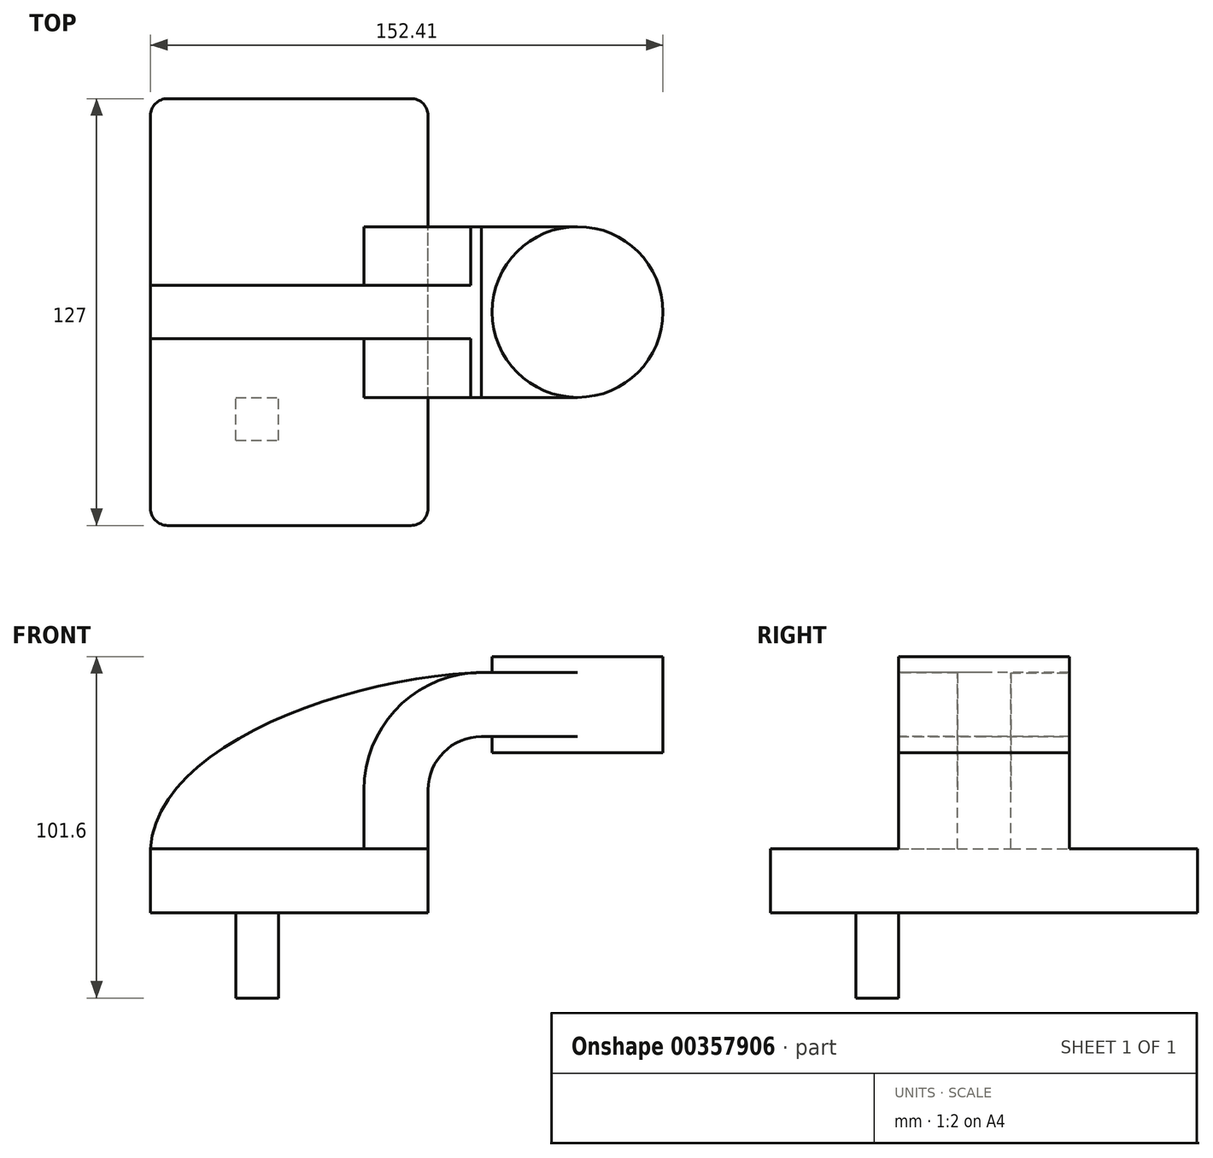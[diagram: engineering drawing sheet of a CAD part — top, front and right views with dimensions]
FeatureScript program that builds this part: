
annotation { "Feature Type Name" : "Feature", "Feature Type Description" : "" }
export const myFeature = defineFeature(function(context is Context, id is Id, definition is map)
    precondition{}
    {
        {
            var Q0;
            Q0=qCreatedBy(makeId("Front.planeOp"),FACE);
            var sketch = newSketch(context, id + "F0", { "sketchPlane" : qUnion([Q0])});
            skLineSegment(sketch, "E0.rect.bottom", {"start": v(-41.28, 9.52) * mm, "end": v(41.28, 9.52) * mm});
            skLineSegment(sketch, "E0.rect.top", {"start": v(-41.28, -9.52) * mm, "end": v(41.28, -9.52) * mm});
            skLineSegment(sketch, "E0.rect.left", {"start": v(-41.28, 9.52) * mm, "end": v(-41.28, -9.52) * mm});
            skLineSegment(sketch, "E0.rect.right", {"start": v(41.28, 9.52) * mm, "end": v(41.28, -9.52) * mm});
            skPoint(sketch, "E0.rect.middle", {"position": v(0, 0) * mm});
            skLineSegment(sketch, "E1", {"start": v(41.28, 9.52) * mm, "end": v(41.28, 27) * mm});
            skArc(sketch, "E2", {"start": v(41.28, 27) * mm, "mid": v(45.92, 38.23) * mm, "end": v(57.15, 42.88) * mm});
            skLineSegment(sketch, "E3", {"start": v(57.15, 42.88) * mm, "end": v(85.72, 42.88) * mm});
            skLineSegment(sketch, "E4.rect.bottom", {"start": v(60.32, 38.1) * mm, "end": v(111.12, 38.1) * mm});
            skLineSegment(sketch, "E4.rect.top", {"start": v(60.32, 66.68) * mm, "end": v(111.12, 66.68) * mm});
            skLineSegment(sketch, "E4.rect.left", {"start": v(60.32, 38.1) * mm, "end": v(60.32, 66.68) * mm});
            skLineSegment(sketch, "E4.rect.right", {"start": v(111.13, 38.1) * mm, "end": v(111.12, 66.68) * mm});
            skPoint(sketch, "E4.rect.middle", {"position": v(85.72, 52.39) * mm});
            skLineSegment(sketch, "E5.0", {"start": v(57.15, 61.93) * mm, "end": v(85.72, 61.93) * mm});
            skArc(sketch, "E5.1", {"start": v(22.23, 27) * mm, "mid": v(32.45, 51.7) * mm, "end": v(57.15, 61.93) * mm});
            skLineSegment(sketch, "E5.2", {"start": v(22.23, 9.52) * mm, "end": v(22.23, 27) * mm});
            skLineSegment(sketch, "E6", {"start": v(85.72, 38.1) * mm, "end": v(85.72, 66.68) * mm});
            skFitSpline(sketch, "E7", {"points": [v(-41.28, 9.53) * mm, v(57.15, 61.93) * mm], "startDerivative": vector(5.2, 92.34) * mm, "endDerivative": vector(120.92, 4.22) * mm});
            skSolve(sketch);
        }
        {
            var Q0;
            Q0=makeQuery(id+"F0.imprint","IMPRINT",FACE,{"disambiguationData":[TD([[makeQuery(id+"F0.imprint","IMPRINT",EDGE,{"derivedFrom":sQuery(id+"F0.wireOp",EDGE,"E0.rect.top")}),1.0]])]});
            extrude(context, id + "F1", {"entities" : qUnion([Q0]), "endBound" : BoundingType.SYMMETRIC, "depth" : 127 * mm});
        }
        {
            var Q0;
            {var subQ9=sQuery(id+"F0.wireOp",EDGE,"E1");Q0=makeQuery(id+"F0.imprint","IMPRINT",FACE,{"disambiguationData":[TD([[makeQuery(id+"F0.imprint","IMPRINT",EDGE,{"derivedFrom":subQ9}),1.0]])]});}
            var Q1;
            {var subQ0=sQuery(id+"F0.wireOp",EDGE,"E6");var subQ1=sQuery(id+"F0.wireOp",EDGE,"E3");var subQ2=makeQuery(id+"F0.imprint","INTERSECT",VERTEX,{"derivedFrom":[subQ1,subQ0]});Q1=makeQuery(id+"F0.imprint","IMPRINT",FACE,{"disambiguationData":[TD([[makeQuery(id+"F0.imprint","IMPRINT",EDGE,{"disambiguationData":[TD([[subQ2,1.0]])],"derivedFrom":subQ1}),1.0]])]});}
            extrude(context, id + "F2", {"entities" : qUnion([Q0, Q1]), "operationType" : NewBodyOperationType.ADD, "endBound" : BoundingType.SYMMETRIC, "depth" : 50.8 * mm});
        }
        {
            var Q0;
            {var subQ3=sQuery(id+"F0.wireOp",EDGE,"E5.2");Q0=makeQuery(id+"F0.imprint","IMPRINT",FACE,{"disambiguationData":[TD([[makeQuery(id+"F0.imprint","IMPRINT",EDGE,{"derivedFrom":subQ3}),1.0]])]});}
            extrude(context, id + "F3", {"entities" : qUnion([Q0]), "operationType" : NewBodyOperationType.ADD, "endBound" : BoundingType.SYMMETRIC, "depth" : 15.88 * mm});
        }
        {
            var Q0;
            {var subQ5=sQuery(id+"F0.wireOp",EDGE,"E4.rect.right");Q0=makeQuery(id+"F0.imprint","IMPRINT",FACE,{"disambiguationData":[TD([[makeQuery(id+"F0.imprint","IMPRINT",EDGE,{"derivedFrom":subQ5}),1.0]])]});}
            var Q1;
            Q1=sQuery(id+"F0.wireOp",EDGE,"E6");
            revolve(context, id + "F4", {"operationType" : NewBodyOperationType.ADD, "entities" : qUnion([Q0]), "axis" : qUnion([Q1]), "revolveType" : RevolveType.FULL});
        }
        {
            var Q0;
            Q0=makeQuery(id+"F1.opExtrude","CAP_EDGE",EDGE,{"disambiguationData":[OSD([sQuery(id+"F0.wireOp",EDGE,"E0.rect.right")])],"isStart":false});
            var Q1;
            Q1=makeQuery(id+"F1.opExtrude","CAP_EDGE",EDGE,{"disambiguationData":[OSD([sQuery(id+"F0.wireOp",EDGE,"E0.rect.left")])],"isStart":false});
            var Q2;
            Q2=makeQuery(id+"F1.opExtrude","CAP_EDGE",EDGE,{"disambiguationData":[OSD([sQuery(id+"F0.wireOp",EDGE,"E0.rect.right")])],"isStart":true});
            var Q3;
            Q3=makeQuery(id+"F1.opExtrude","CAP_EDGE",EDGE,{"disambiguationData":[OSD([sQuery(id+"F0.wireOp",EDGE,"E0.rect.left")])],"isStart":true});
            fillet(context, id + "F5", {"entities" : qUnion([Q0, Q1, Q2, Q3]), "radius" : 5.08 * mm, "tangentPropagation" : true, "allowEdgeOverflow" : false});
        }
        {
            var Q0;
            Q0=makeQuery(id+"F1.opExtrude","SWEPT_FACE",FACE,{"disambiguationData":[OSD([sQuery(id+"F0.wireOp",EDGE,"E0.rect.top")])]});
            var sketch = newSketch(context, id + "F6", { "sketchPlane" : qUnion([Q0])});
            skLineSegment(sketch, "E8.bottom", {"start": v(-15.88, 38.1) * mm, "end": v(-3.18, 38.1) * mm});
            skLineSegment(sketch, "E8.top", {"start": v(-15.88, 25.4) * mm, "end": v(-3.18, 25.4) * mm});
            skLineSegment(sketch, "E8.left", {"start": v(-15.88, 38.1) * mm, "end": v(-15.88, 25.4) * mm});
            skLineSegment(sketch, "E8.right", {"start": v(-3.18, 38.1) * mm, "end": v(-3.18, 25.4) * mm});
            skSolve(sketch);
        }
        {
            var Q0;
            Q0=makeQuery(id+"F6.imprint","IMPRINT",FACE,{"disambiguationData":[TD([[makeQuery(id+"F6.imprint","IMPRINT",EDGE,{"derivedFrom":sQuery(id+"F6.wireOp",EDGE,"E8.bottom")}),-1.0]])]});
            extrude(context, id + "F7", {"entities" : qUnion([Q0]), "operationType" : NewBodyOperationType.ADD, "depth" : 25.4 * mm, "offsetDistance" : 25.4 * mm});
        }
    });
